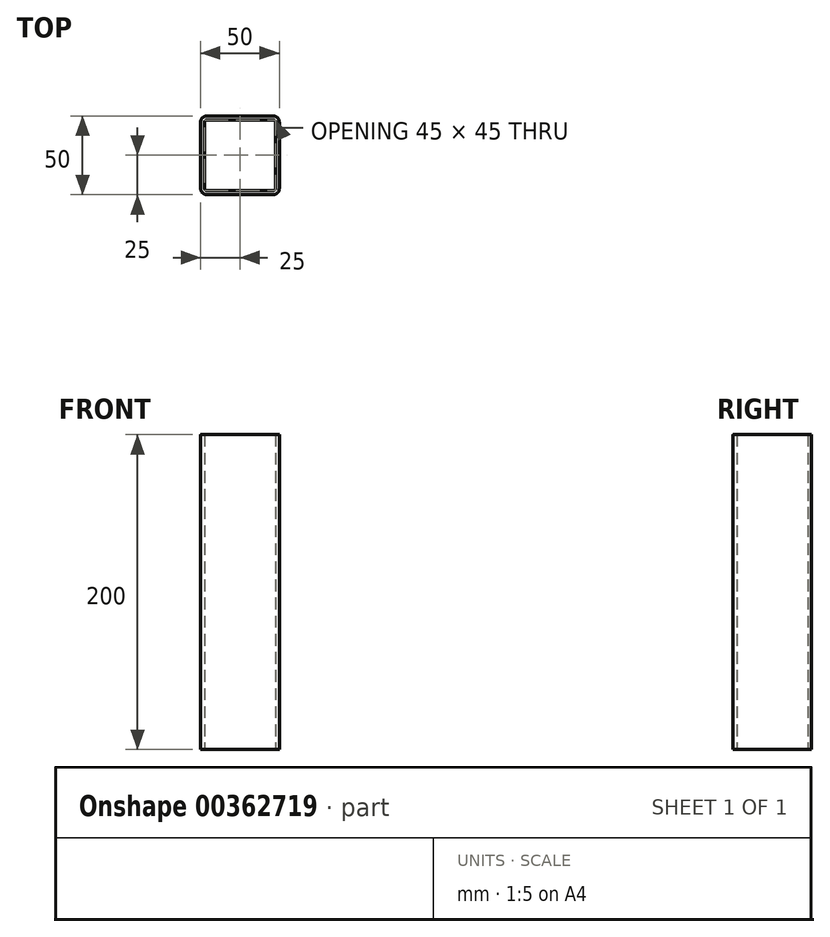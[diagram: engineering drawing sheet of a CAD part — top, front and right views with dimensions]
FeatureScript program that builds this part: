
annotation { "Feature Type Name" : "Feature", "Feature Type Description" : "" }
export const myFeature = defineFeature(function(context is Context, id is Id, definition is map)
    precondition{}
    {
        {
            var Q0;
            Q0=qCreatedBy(makeId("Top.planeOp"),FACE);
            var sketch = newSketch(context, id + "F0", { "sketchPlane" : qUnion([Q0])});
            skLineSegment(sketch, "E0.bottom", {"start": v(-21, 25) * mm, "end": v(21, 25) * mm});
            skLineSegment(sketch, "E0.top", {"start": v(-21, -25) * mm, "end": v(21, -25) * mm});
            skLineSegment(sketch, "E0.left", {"start": v(-25, 21) * mm, "end": v(-25, -21) * mm});
            skLineSegment(sketch, "E0.right", {"start": v(25, 21) * mm, "end": v(25, -21) * mm});
            skPoint(sketch, "E0.middle", {"position": v(0, 0) * mm});
            skPoint(sketch, "E1.visualSharp", {"position": v(25, 25) * mm});
            skArc(sketch, "E1.filletArc", {"start": v(25, 21) * mm, "mid": v(23.83, 23.83) * mm, "end": v(21, 25) * mm});
            skPoint(sketch, "E2.visualSharp", {"position": v(-25, 25) * mm});
            skArc(sketch, "E2.filletArc", {"start": v(-21, 25) * mm, "mid": v(-23.83, 23.83) * mm, "end": v(-25, 21) * mm});
            skPoint(sketch, "E3.visualSharp", {"position": v(-25, -25) * mm});
            skArc(sketch, "E3.filletArc", {"start": v(-25, -21) * mm, "mid": v(-23.83, -23.83) * mm, "end": v(-21, -25) * mm});
            skPoint(sketch, "E4.visualSharp", {"position": v(25, -25) * mm});
            skArc(sketch, "E4.filletArc", {"start": v(21, -25) * mm, "mid": v(23.83, -23.83) * mm, "end": v(25, -21) * mm});
            skArc(sketch, "E5.0", {"start": v(-21, 22.5) * mm, "mid": v(-22.06, 22.06) * mm, "end": v(-22.5, 21) * mm});
            skLineSegment(sketch, "E5.1", {"start": v(-22.5, 21) * mm, "end": v(-22.5, -21) * mm});
            skLineSegment(sketch, "E5.2", {"start": v(-21, 22.5) * mm, "end": v(21, 22.5) * mm});
            skArc(sketch, "E5.3", {"start": v(-22.5, -21) * mm, "mid": v(-22.06, -22.06) * mm, "end": v(-21, -22.5) * mm});
            skArc(sketch, "E5.4", {"start": v(22.5, 21) * mm, "mid": v(22.06, 22.06) * mm, "end": v(21, 22.5) * mm});
            skLineSegment(sketch, "E5.5", {"start": v(22.5, 21) * mm, "end": v(22.5, -21) * mm});
            skArc(sketch, "E5.6", {"start": v(21, -22.5) * mm, "mid": v(22.06, -22.06) * mm, "end": v(22.5, -21) * mm});
            skLineSegment(sketch, "E5.7", {"start": v(-21, -22.5) * mm, "end": v(21, -22.5) * mm});
            skSolve(sketch);
        }
        {
            var Q0;
            Q0 = qSketchRegion(id + "F0", true);
            extrude(context, id + "F1", {"entities" : qUnion([Q0]), "depth" : 200 * mm});
        }
    });
